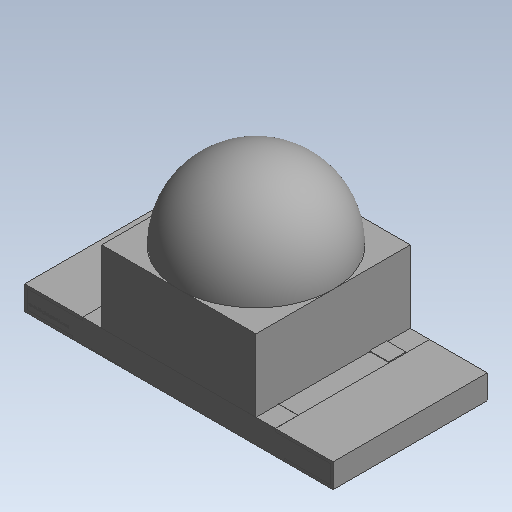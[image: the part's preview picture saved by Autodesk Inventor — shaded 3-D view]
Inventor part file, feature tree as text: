
AUTODESK INVENTOR PART (.ipt)
format: ipt  version: 2020 (Build 240168000, 168)  size: 552,448 bytes
history: native  units: mm (DEFAULTED — no unit token found)
features: extrude x7, revolve x1, other x1
ambient origin geometry x8: Origin, YZ Plane, XZ Plane, XY Plane, X Axis, Y Axis, Z Axis, Center Point
bodies: Solid1 (feature_tree), Solid2 (feature_tree), Solid3 (feature_tree), Solid4 (feature_tree), Solid5 (feature_tree), Solid6 (feature_tree), Solid7 (feature_tree), Solid8 (feature_tree), Solid9 (feature_tree)
feature tree (9):
  revolve  "Revolve1"  [1 undecoded]
  extrude  "Extrude2[1]"  [1 undecoded]
  extrude  "Extrude2[2]"  [1 undecoded]
  extrude  "Extrude3"  [1 undecoded]
  extrude  "Extrude4[1]"  [1 undecoded]
  extrude  "Extrude4[2]"  [1 undecoded]
  extrude  "Extrude6"  [1 undecoded]
  other  "Cut-Extrude1"
  extrude  "Extrude7"  [1 undecoded]
note: 8 required parameter values undecoded (feature->parameter linkage not recoverable at this tier; creation-order binding heuristic only, values carry confidence <= 0.55)
